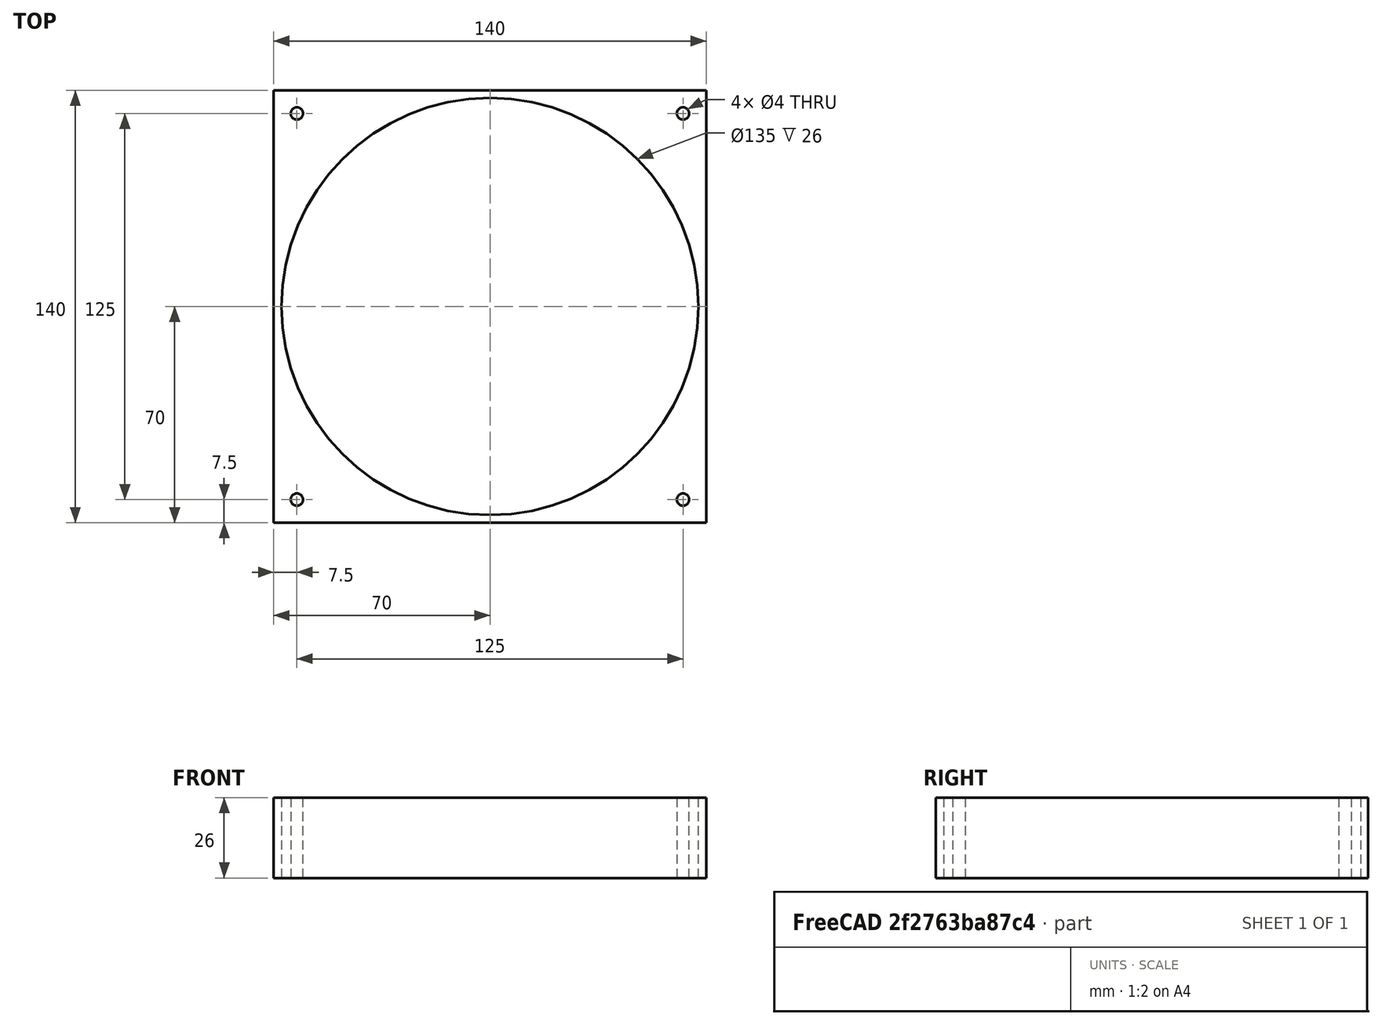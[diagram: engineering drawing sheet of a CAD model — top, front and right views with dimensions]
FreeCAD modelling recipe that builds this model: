
FCSTD DOCUMENT  (FreeCAD 0.19R)
Label: ek-vardar-140
License: All rights reserved
LicenseURL: http://en.wikipedia.org/wiki/All_rights_reserved
objects: PartDesign::CoordinateSystem×2, App::DocumentObjectGroup×2, App::FeaturePython×1, App::Part×1, Sketcher::SketchObject×1, PartDesign::Pad×1, PartDesign::Body×1
note: 6 computed .brp shape members not serialized (recipe doc carries the construction recipe); baked Part::Feature solids carry a one-line shape summary decoded from their .brp

FEATURE [PartDesign::CoordinateSystem] LCS_Origin
  AttacherType = Attacher::AttachEngine3D
  MapMode = 2
  Support = -> [X_Axis]
FEATURE [App::DocumentObjectGroup] Constraints
FEATURE [App::FeaturePython] Variables  # WARN: FeaturePython — macro-defined, semantics opaque (R4)
FEATURE [App::Part] Model
  Configuration = 0
  Group = -> [LCS_Origin,Constraints,Variables]
  Origin = -> Origin
  Type = Assembly4 Model
FEATURE [PartDesign::CoordinateSystem] LCS_0
  AttacherType = Attacher::AttachEngine3D
  MapMode = 2
  Support = -> [X_Axis001]
FEATURE [Sketcher::SketchObject] Sketch_1
  expr: Constraints[11] = 140 - 5
  sketch-geometry (15):
    g0: LineSegment StartX=0 StartY=0 StartZ=0 EndX=140 EndY=0 EndZ=0
    g1: LineSegment StartX=140 StartY=0 StartZ=0 EndX=140 EndY=140 EndZ=0
    g2: LineSegment StartX=140 StartY=140 StartZ=0 EndX=0 EndY=140 EndZ=0
    g3: LineSegment StartX=0 StartY=140 StartZ=0 EndX=0 EndY=0 EndZ=0
    g4: Circle CenterX=70 CenterY=70 CenterZ=0 NormalX=0 NormalY=0 NormalZ=1 AngleXU=0 Radius=67.5
    g5: LineSegment [constr] StartX=0 StartY=140 StartZ=0 EndX=140 EndY=0 EndZ=0
    g6: GeomPoint X=7.5 Y=70 Z=0
    g7: Circle CenterX=7.5 CenterY=132.5 CenterZ=0 NormalX=0 NormalY=0 NormalZ=1 AngleXU=0 Radius=2
    g8: Circle CenterX=132.5 CenterY=132.5 CenterZ=0 NormalX=0 NormalY=0 NormalZ=1 AngleXU=0 Radius=2
    g9: LineSegment [constr] StartX=7.5 StartY=132.5 StartZ=0 EndX=132.5 EndY=132.5 EndZ=0
    g10: Circle CenterX=7.5 CenterY=7.5 CenterZ=0 NormalX=0 NormalY=0 NormalZ=1 AngleXU=0 Radius=2
    g11: LineSegment [constr] StartX=7.5 StartY=132.5 StartZ=0 EndX=7.5 EndY=7.5 EndZ=0
    g12: Circle CenterX=132.5 CenterY=7.5 CenterZ=0 NormalX=0 NormalY=0 NormalZ=1 AngleXU=0 Radius=2
    g13: LineSegment [constr] StartX=7.5 StartY=7.5 StartZ=0 EndX=132.5 EndY=7.5 EndZ=0
    g14: LineSegment [constr] StartX=7.5 StartY=70 StartZ=0 EndX=70 EndY=70 EndZ=0
  constraints (36):
    c: Coincident(g0,g1)
    c: Coincident(g1,g2)
    c: Coincident(g2,g3)
    c: Coincident(g3,g0)
    c: Horizontal(g0)
    c: Horizontal(g2)
    c: Vertical(g1)
    c: Vertical(g3)
    c: Coincident(g0,g-1)
    c: Equal(g2,g3)
    c: Distance(g2) = 140
    c: Diameter(g4) = 135
    c: Coincident(g5,g2)
    c: Coincident(g5,g0)
    c: Symmetric(g5,g5,g4)
    c: Diameter(g7) = 4
    c: PointOnObject(g7,g5)
    c: Equal(g7,g8) = 4
    c: Coincident(g7,g9)
    c: Coincident(g8,g9)
    c: Distance(g9) = 125
    c: Equal(g7,g10) = 4
    c: Coincident(g7,g11)
    c: Coincident(g10,g11)
    c: Equal(g11,g9)
    c: Perpendicular(g11,g9)
    c: Equal(g7,g12) = 4
    c: Coincident(g10,g13)
    c: Coincident(g12,g13)
    c: Equal(g9,g13)
    c: Parallel(g13,g9)
    c: Horizontal(g9)
    c: Symmetric(g11,g11,g6)
    c: Coincident(g14,g6)
    c: Coincident(g14,g4)
    c: Horizontal(g14)
FEATURE [PartDesign::Pad] Pad
  Direction = (1,1,1)
  Length = 26
  Length2 = 100
  Profile = -> Sketch_1
  Type = 0
FEATURE [PartDesign::Body] Body
  Group = -> [LCS_0,Pad]
  Origin = -> Origin001
  Tip = -> Pad
FEATURE [App::DocumentObjectGroup] Parts
  Group = -> [Body,Sketch_1]
